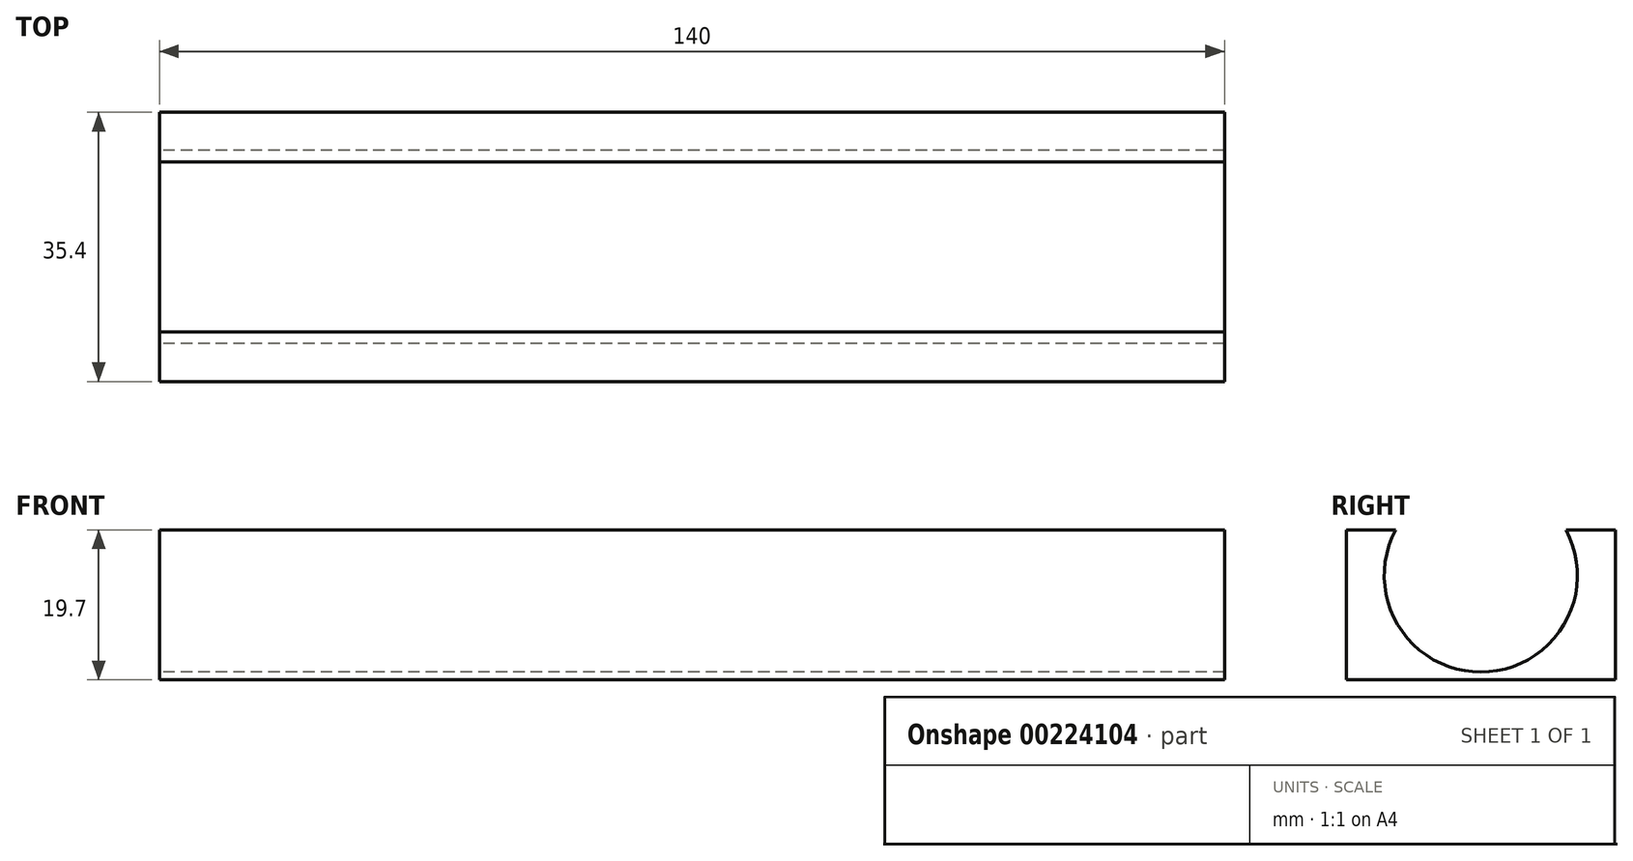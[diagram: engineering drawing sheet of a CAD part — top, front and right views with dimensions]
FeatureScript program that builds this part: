
annotation { "Feature Type Name" : "Feature", "Feature Type Description" : "" }
export const myFeature = defineFeature(function(context is Context, id is Id, definition is map)
    precondition{}
    {
        {
            assignVariable(context, id + "F0", {"name" : "dowel_l", "anyValue" : 140});
        }
        {
            var Q0;
            Q0=qCreatedBy(makeId("Right.planeOp"),FACE);
            var sketch = newSketch(context, id + "F1", { "sketchPlane" : qUnion([Q0])});
            skCircle(sketch, "E0", {"center": v(0, 0) * mm, "radius": 12.7 * mm});
            skSolve(sketch);
        }
        {
            var Q0;
            Q0 = qSketchRegion(id + "F1", true);
            extrude(context, id + "F2", {"entities" : qUnion([Q0]), "depth" : (getVariable(context, 'dowel_l') / 2) * mm, "hasSecondDirection" : true, "secondDirectionOppositeDirection" : true, "secondDirectionDepth" : (getVariable(context, 'dowel_l') / 2) * mm});
        }
        {
            var Q0;
            Q0=qCreatedBy(makeId("Right.planeOp"),FACE);
            var sketch = newSketch(context, id + "F3", { "sketchPlane" : qUnion([Q0])});
            skLineSegment(sketch, "E1.bottom", {"start": v(-17.7, 6) * mm, "end": v(17.7, 6) * mm});
            skLineSegment(sketch, "E1.top", {"start": v(-17.7, -13.7) * mm, "end": v(17.7, -13.7) * mm});
            skLineSegment(sketch, "E1.left", {"start": v(-17.7, 6) * mm, "end": v(-17.7, -13.7) * mm});
            skLineSegment(sketch, "E1.right", {"start": v(17.7, 6) * mm, "end": v(17.7, -13.7) * mm});
            skPoint(sketch, "E2", {"position": v(0, 6) * mm});
            skSolve(sketch);
        }
        {
            var Q0;
            Q0 = qSketchRegion(id + "F3", true);
            var Q1;
            Q1=makeQuery(id+"F2.opExtrude","CAP_FACE",FACE,{"disambiguationData":[OSD([sQuery(id+"F1.wireOp",EDGE,"E0")])],"isStart":false});
            var Q2;
            Q2=makeQuery(id+"F2.opExtrude","SWEPT_BODY",BODY,{"disambiguationData":[OSD([sQuery(id+"F1.wireOp",EDGE,"E0")])]});
            var Q3;
            Q3=makeQuery(id+"F2.opExtrude","CAP_FACE",FACE,{"disambiguationData":[OSD([sQuery(id+"F1.wireOp",EDGE,"E0")])],"isStart":true});
            extrude(context, id + "F4", {"entities" : qUnion([Q0]), "endBound" : BoundingType.UP_TO_SURFACE, "endBoundEntityFace" : qUnion([Q1]), "endBoundEntityBody" : qUnion([Q2]), "depth" : 25 * mm, "hasSecondDirection" : true, "secondDirectionBound" : SecondDirectionBoundingType.UP_TO_SURFACE, "secondDirectionOppositeDirection" : true, "secondDirectionBoundEntityFace" : qUnion([Q3]), "secondDirectionDepth" : 25 * mm});
        }
        {
            var Q0;
            Q0=makeQuery(id+"F2.opExtrude","SWEPT_BODY",BODY,{"disambiguationData":[OSD([sQuery(id+"F1.wireOp",EDGE,"E0")])]});
            var Q1;
            Q1=makeQuery(id+"F4.opExtrude","SWEPT_BODY",BODY,{"disambiguationData":[OSD([sQuery(id+"F3.wireOp",EDGE,"E1.bottom"),sQuery(id+"F3.wireOp",EDGE,"E1.top"),sQuery(id+"F3.wireOp",EDGE,"E1.left"),sQuery(id+"F3.wireOp",EDGE,"E1.right")])]});
            booleanBodies(context, id + "F5", {"operationType" : BooleanOperationType.SUBTRACTION, "tools" : qUnion([Q0]), "targets" : qUnion([Q1])});
        }
    });
